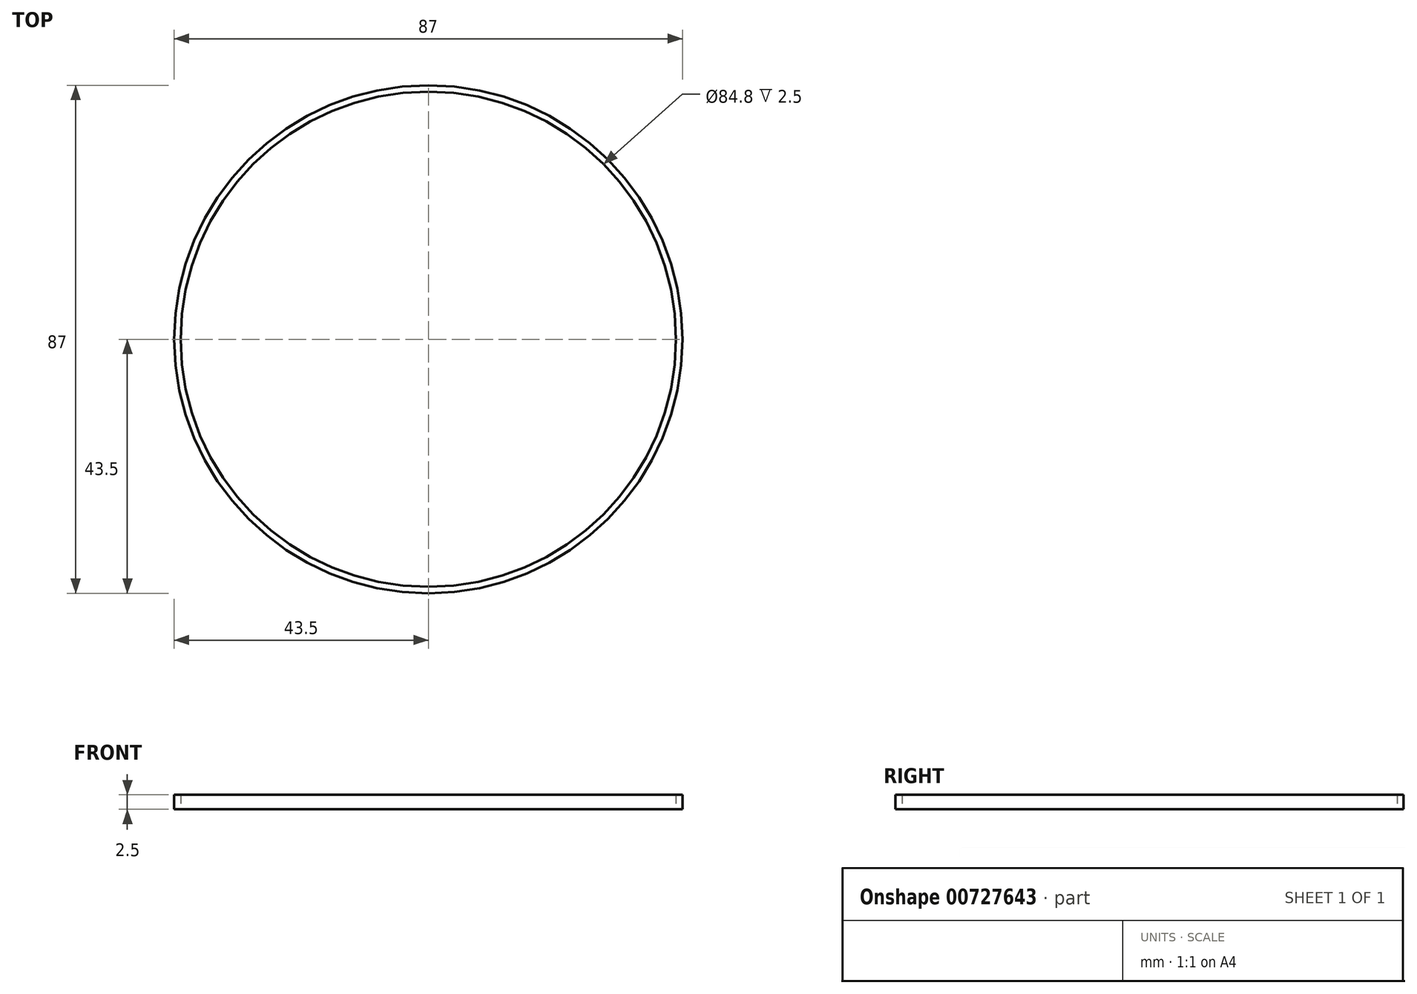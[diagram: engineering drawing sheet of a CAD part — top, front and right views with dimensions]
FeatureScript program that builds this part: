
annotation { "Feature Type Name" : "Feature", "Feature Type Description" : "" }
export const myFeature = defineFeature(function(context is Context, id is Id, definition is map)
    precondition{}
    {
        {
            var Q0;
            Q0=qCreatedBy(makeId("Top.planeOp"),FACE);
            var sketch = newSketch(context, id + "F0", { "sketchPlane" : qUnion([Q0])});
            skCircle(sketch, "E0", {"center": v(0, 0) * mm, "radius": 42.4 * mm});
            skCircle(sketch, "E1", {"center": v(0, 0) * mm, "radius": 43.5 * mm});
            skSolve(sketch);
        }
        {
            var Q0;
            Q0=makeQuery(id+"F0.imprint","IMPRINT",FACE,{"disambiguationData":[TD([[makeQuery(id+"F0.imprint","IMPRINT",EDGE,{"derivedFrom":sQuery(id+"F0.wireOp",EDGE,"E0")}),-1.0]])]});
            extrude(context, id + "F1", {"entities" : qUnion([Q0]), "depth" : 2.5 * mm, "offsetDistance" : 25 * mm});
        }
    });
